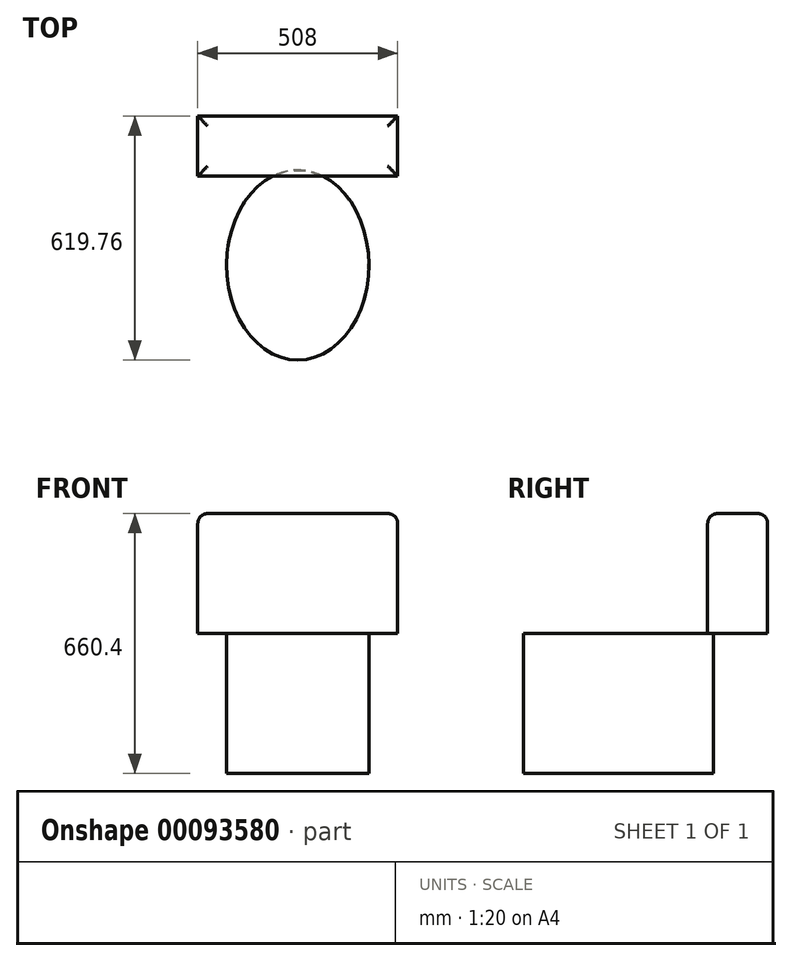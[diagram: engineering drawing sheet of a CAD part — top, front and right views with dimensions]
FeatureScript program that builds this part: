
annotation { "Feature Type Name" : "Feature", "Feature Type Description" : "" }
export const myFeature = defineFeature(function(context is Context, id is Id, definition is map)
    precondition{}
    {
        {
            var Q0;
            Q0=qCreatedBy(makeId("Top.planeOp"),FACE);
            var sketch = newSketch(context, id + "F0", { "sketchPlane" : qUnion([Q0])});
            skLineSegment(sketch, "E0", {"start": v(0, 0) * mm, "end": v(0, -482.6) * mm, "construction": true});
            skEllipse(sketch, "E1", {"center": v(0, -241.3) * mm, "majorRadius": 241.3 * mm, "minorRadius": 180.6 * mm, "majorAxis": v(0, -1)});
            skSolve(sketch);
        }
        {
            var Q0;
            Q0 = qSketchRegion(id + "F0", true);
            extrude(context, id + "F1", {"entities" : qUnion([Q0]), "oppositeDirection" : true, "depth" : 355.6 * mm});
        }
        {
            var Q0;
            Q0=makeQuery(id+"F1.opExtrude","CAP_FACE",FACE,{"disambiguationData":[OSD([sQuery(id+"F0.wireOp",EDGE,"E1")])],"isStart":true});
            var sketch = newSketch(context, id + "F2", { "sketchPlane" : qUnion([Q0])});
            skLineSegment(sketch, "E2.bottom", {"start": v(254, -15.24) * mm, "end": v(-254, -15.24) * mm});
            skLineSegment(sketch, "E2.top", {"start": v(254, 137.16) * mm, "end": v(-254, 137.16) * mm});
            skLineSegment(sketch, "E2.left", {"start": v(254, -15.24) * mm, "end": v(254, 137.16) * mm});
            skLineSegment(sketch, "E2.right", {"start": v(-254, -15.24) * mm, "end": v(-254, 137.16) * mm});
            skPoint(sketch, "E2.middle", {"position": v(0, 60.96) * mm});
            skSolve(sketch);
        }
        {
            var Q0;
            Q0 = qSketchRegion(id + "F2", true);
            extrude(context, id + "F3", {"entities" : qUnion([Q0]), "operationType" : NewBodyOperationType.ADD, "depth" : 304.8 * mm});
        }
        {
            var Q0;
            Q0=makeQuery(id+"F3.opExtrude","CAP_EDGE",EDGE,{"disambiguationData":[OSD([sQuery(id+"F2.wireOp",EDGE,"E2.bottom")])],"isStart":false});
            var Q1;
            Q1=makeQuery(id+"F3.opExtrude","CAP_EDGE",EDGE,{"disambiguationData":[OSD([sQuery(id+"F2.wireOp",EDGE,"E2.left")])],"isStart":false});
            var Q2;
            Q2=makeQuery(id+"F3.opExtrude","CAP_EDGE",EDGE,{"disambiguationData":[OSD([sQuery(id+"F2.wireOp",EDGE,"E2.top")])],"isStart":false});
            var Q3;
            Q3=makeQuery(id+"F3.opExtrude","CAP_EDGE",EDGE,{"disambiguationData":[OSD([sQuery(id+"F2.wireOp",EDGE,"E2.right")])],"isStart":false});
            fillet(context, id + "F4", {"entities" : qUnion([Q0, Q1, Q2, Q3]), "radius" : 25.4 * mm, "tangentPropagation" : true, "allowEdgeOverflow" : false});
        }
    });
